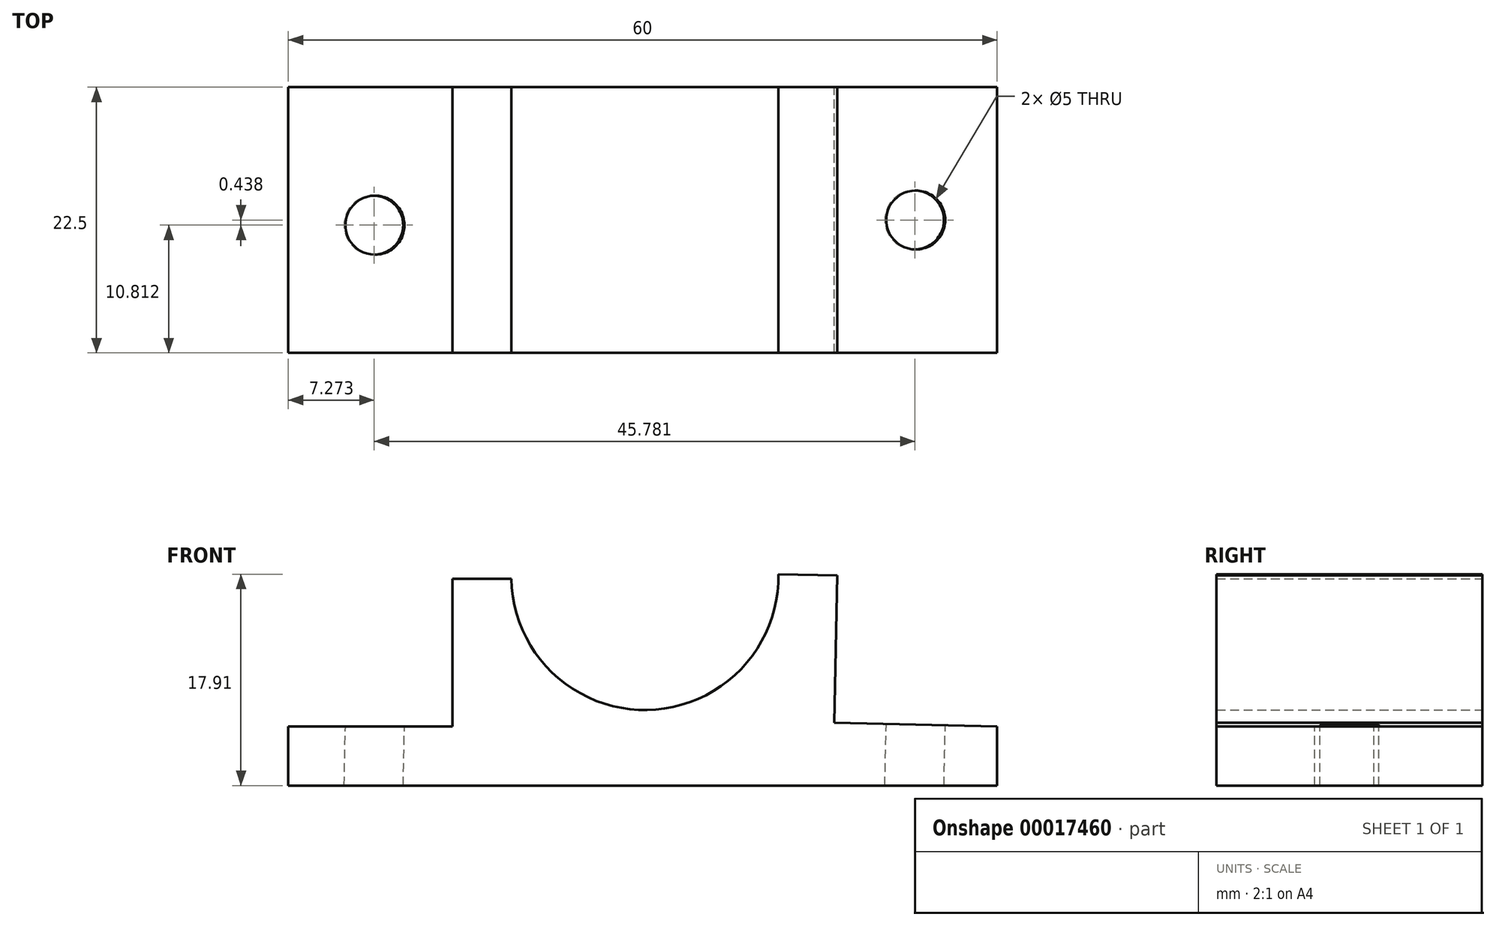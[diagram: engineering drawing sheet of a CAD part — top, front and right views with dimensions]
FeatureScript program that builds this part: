
annotation { "Feature Type Name" : "Feature", "Feature Type Description" : "" }
export const myFeature = defineFeature(function(context is Context, id is Id, definition is map)
    precondition{}
    {
        {
            var Q0;
            Q0=qCreatedBy(makeId("Front.planeOp"),FACE);
            var sketch = newSketch(context, id + "F0", { "sketchPlane" : qUnion([Q0])});
            skLineSegment(sketch, "E0", {"start": v(-60, 0) * mm, "end": v(0, 0) * mm});
            skLineSegment(sketch, "E1", {"start": v(-60, 0) * mm, "end": v(-60, 5) * mm});
            skLineSegment(sketch, "E2", {"start": v(-60, 5) * mm, "end": v(-46.12, 5) * mm});
            skLineSegment(sketch, "E3", {"start": v(-46.12, 5) * mm, "end": v(-46.12, 17.5) * mm});
            skLineSegment(sketch, "E4", {"start": v(-46.12, 17.5) * mm, "end": v(-41.12, 17.5) * mm});
            skLineSegment(sketch, "E5", {"start": v(0, 0) * mm, "end": v(0, 5) * mm});
            skLineSegment(sketch, "E6", {"start": v(-13.78, 5.3) * mm, "end": v(-13.52, 17.8) * mm});
            skArc(sketch, "E7", {"start": v(-41.12, 17.5) * mm, "mid": v(-29.62, 6.4) * mm, "end": v(-18.52, 17.9) * mm});
            skLineSegment(sketch, "E8", {"start": v(0, 5) * mm, "end": v(0, 0) * mm});
            skLineSegment(sketch, "E9", {"start": v(0, 0) * mm, "end": v(-60, 0) * mm});
            skLineSegment(sketch, "E10", {"start": v(-18.52, 17.9) * mm, "end": v(-13.52, 17.8) * mm});
            skLineSegment(sketch, "E11", {"start": v(0, 5) * mm, "end": v(-13.78, 5.3) * mm});
            skSolve(sketch);
        }
        {
            var Q0;
            Q0=makeQuery(id+"F0.imprint","IMPRINT",FACE,{"disambiguationData":[TD([[makeQuery(id+"F0.imprint","IMPRINT",EDGE,{"derivedFrom":sQuery(id+"F0.wireOp",EDGE,"E1")}),-1.0]])]});
            extrude(context, id + "F1", {"entities" : qUnion([Q0]), "depth" : 22.5 * mm});
        }
        {
            var Q0;
            Q0=makeQuery(id+"F1.opExtrude","SWEPT_FACE",FACE,{"disambiguationData":[OSD([sQuery(id+"F0.wireOp",EDGE,"E11")])]});
            var sketch = newSketch(context, id + "F2", { "sketchPlane" : qUnion([Q0])});
            skCircle(sketch, "E12", {"center": v(-7, -11.25) * mm, "radius": 2.5 * mm});
            skCircle(sketch, "E13", {"center": v(-52.77, -11.69) * mm, "radius": 2.5 * mm});
            skSolve(sketch);
        }
        {
            var Q0;
            Q0=makeQuery(id+"F2.imprint","IMPRINT",FACE,{"disambiguationData":[TD([[makeQuery(id+"F2.imprint","IMPRINT",EDGE,{"derivedFrom":sQuery(id+"F2.wireOp",EDGE,"E12")}),1.0]])]});
            var Q1;
            Q1=makeQuery(id+"F2.imprint","IMPRINT",FACE,{"disambiguationData":[TD([[makeQuery(id+"F2.imprint","IMPRINT",EDGE,{"derivedFrom":sQuery(id+"F2.wireOp",EDGE,"E13")}),1.0]])]});
            extrude(context, id + "F3", {"entities" : qUnion([Q0, Q1]), "operationType" : NewBodyOperationType.REMOVE, "endBound" : BoundingType.THROUGH_ALL, "oppositeDirection" : true, "depth" : 25 * mm});
        }
    });
